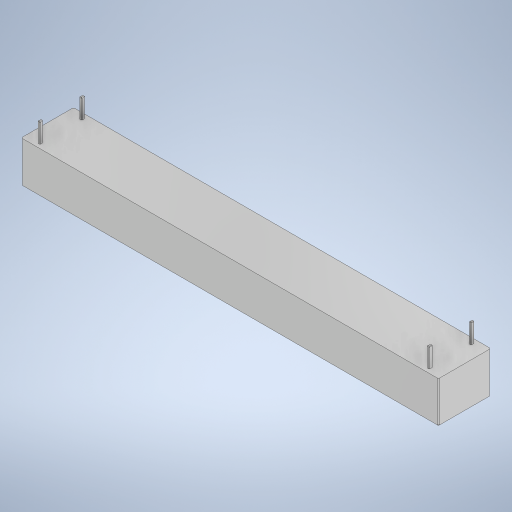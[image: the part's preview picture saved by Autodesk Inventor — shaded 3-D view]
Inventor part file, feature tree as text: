
AUTODESK INVENTOR PART (.ipt)
format: ipt  version: 2023 (Build 270158000, 158)  size: 330,240 bytes
history: native  units: in
note: dims shown in document units (in); Inventor stores cm internally (conversion verified against a paired STEP export)
features: extrude x4, sketch x4, thread x2, chamfer x2
ambient origin geometry x8: Origin, YZ Plane, XZ Plane, XY Plane, X Axis, Y Axis, Z Axis, Center Point
bodies: Solid1 (feature_tree)
feature tree (12):
  extrude  "Extrusion1"  Depth=0.3701in
  extrude  "Extrusion2"  Depth=0.0236in
  extrude  "Extrusion3"  Depth=0.2953in
  extrude  "Extrusion4"  Depth=0.1378in TaperAngle=0.0deg
  thread  "Thread1"  [1 undecoded]
  thread  "Thread2"  [1 undecoded]
  chamfer  "Chamfer1"  Distance=0.1969in
  chamfer  "Chamfer2"  Distance=0.0787in
  sketch  "Sketch3"  dims[d0=2.9528in d1=0.3701in]
  sketch  "Sketch4"  dims[d2=0.2953in d3=0.0in d7=0.0236in]
  sketch  "Sketch5"  dims[d8=0.0157in d9=0.2953in]
  sketch  "Sketch6"  dims[d10=2.7559in d11=0.1378in d12=0.0in d13=2.622in d14=0.0787in d15=0.1969in d16=0.0in d17=0.0787in d18=2.7953in d19=0.1969in d20=0.0in d21=0.1969in d22=0.0in d23=0.1969in d24=0.0in d25=0.0079in d26=0.0787in d27=45.0deg d28=0.0039in d29=0.0787in d30=45.0deg]
note: 2 required parameter values undecoded (feature->parameter linkage not recoverable at this tier; creation-order binding heuristic only, values carry confidence <= 0.55)
